# Revit family: Thorn Chalice Housing
name_source: partatom
category: Leuchten
revit_build: Autodesk Revit 2016 (Build: 20150714_1515(x64)
units: mm (PartAtom-declared; Revit-internal decimal feet)

## family parameters
Basisbauteil = Fläche
Beim Laden mit Abzugskörper schneiden = Nein
Bemaßung runder Anschluss = Durchmesser verwenden
Gemeinsam genutzt = Nein
Lichtquelle = Nein
OmniClass-Nummer = 23.80.70.11
OmniClass-Titel = Luminaries for Internal Lighting
Raumberechnungspunkt = Nein
Teiletyp = Normal

## types (1)
- Thorn Chalice Housing D220
    Baugruppenkennzeichen = D5020200
    Beschreibung = Cylindrical surface-mount housing
    Emissionsform beim Rendern sichtbar = Nein
    Height = 228 mm  [stored 0.748031 ft]
    Hersteller = Thorn Lighting
    Housing = Thorn_Metal_White
    Length = 220 mm  [stored 0.721785 ft]
    Modell = 96628908
    Scheinlast = 0 VA
    URL = http://wwwthornlighting.com
    Vorgabe-Ansicht = 0 mm  [stored 0 ft]
    Width = 220 mm  [stored 0.721785 ft]

note: [stored X ft] marks values corroborated as IEEE doubles in the binary element streams (Revit-internal decimal feet)

## geometry (parser evidence)
native form markers: Sweep x3
no freeform markers — native parametric forms only
